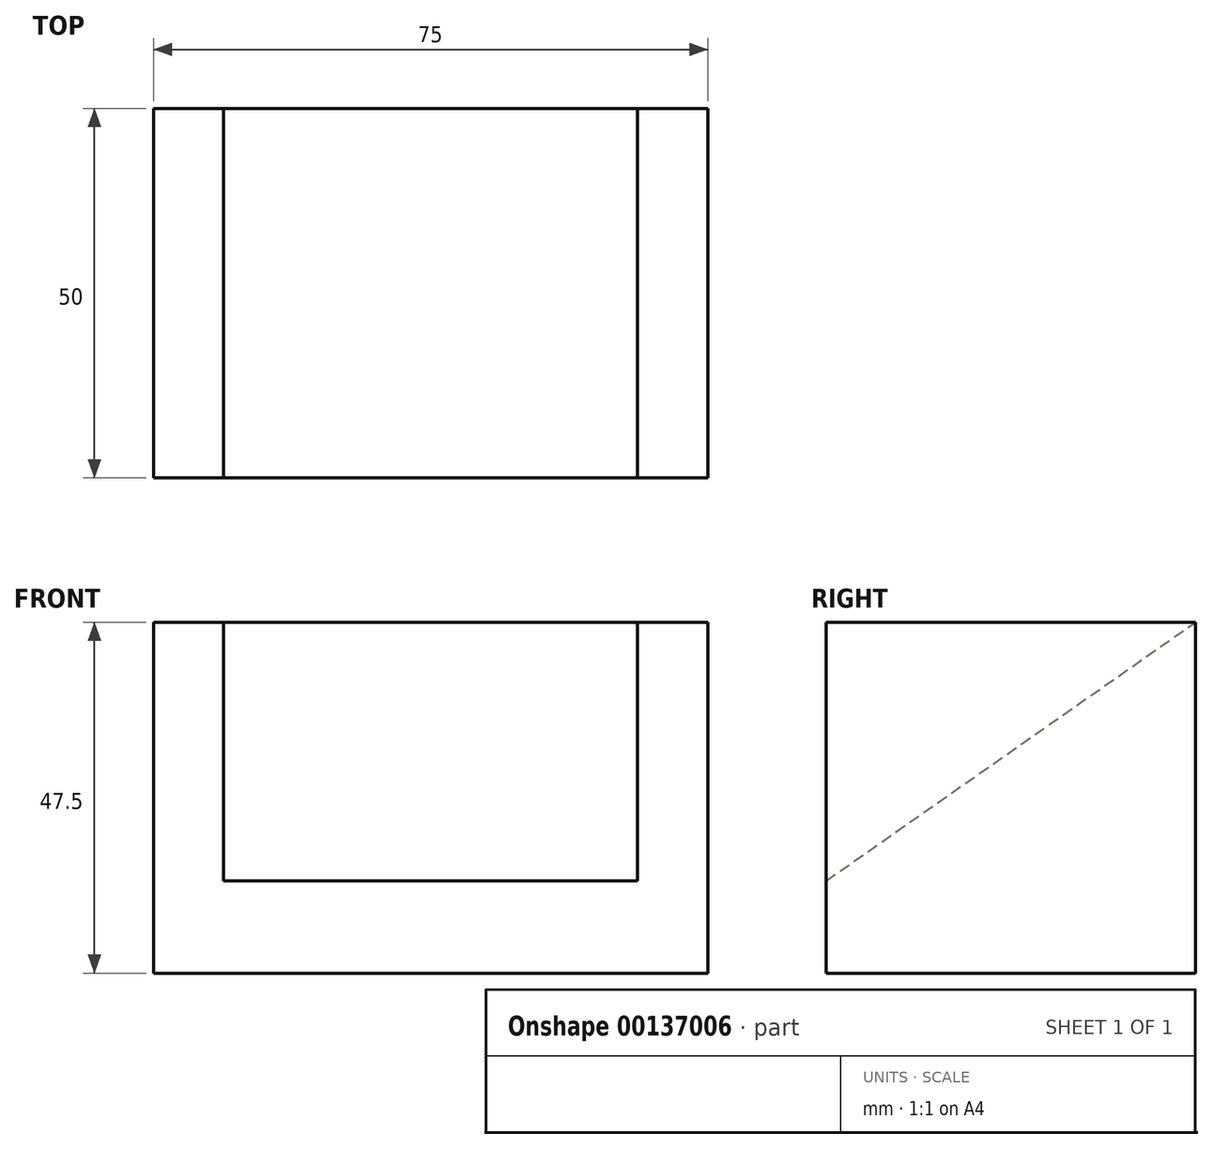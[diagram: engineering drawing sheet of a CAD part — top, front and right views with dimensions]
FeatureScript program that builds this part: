
annotation { "Feature Type Name" : "Feature", "Feature Type Description" : "" }
export const myFeature = defineFeature(function(context is Context, id is Id, definition is map)
    precondition{}
    {
        {
            var Q0;
            Q0=qCreatedBy(makeId("Front.planeOp"),FACE);
            var sketch = newSketch(context, id + "F0", { "sketchPlane" : qUnion([Q0])});
            skLineSegment(sketch, "E0.bottom", {"start": v(0, 0) * mm, "end": v(75, 0) * mm});
            skLineSegment(sketch, "E0.top", {"start": v(0, 47.5) * mm, "end": v(75, 47.5) * mm});
            skLineSegment(sketch, "E0.left", {"start": v(0, 0) * mm, "end": v(0, 47.5) * mm});
            skLineSegment(sketch, "E0.right", {"start": v(75, 0) * mm, "end": v(75, 47.5) * mm});
            skSolve(sketch);
        }
        {
            var Q0;
            Q0 = qSketchRegion(id + "F0", true);
            extrude(context, id + "F1", {"entities" : qUnion([Q0]), "depth" : 50 * mm});
        }
        {
            var Q0;
            Q0=makeQuery(id+"F1.opExtrude","CAP_EDGE",EDGE,{"disambiguationData":[OSD([sQuery(id+"F0.wireOp",EDGE,"E0.top")])],"isStart":true});
            cPlane(context, id + "F2", {"entities" : qUnion([Q0]), "cplaneType" : CPlaneType.LINE_ANGLE, "offset" : 25 * mm, "angle" : 35 * degree, "width" : 150 * mm, "height" : 150 * mm});
        }
        {
            var Q0;
            Q0=qCreatedBy(id+"F2.planeOp",FACE);
            var sketch = newSketch(context, id + "F3", { "sketchPlane" : qUnion([Q0])});
            skLineSegment(sketch, "E1.bottom", {"start": v(-65.5, 78.9) * mm, "end": v(-9.5, 78.9) * mm});
            skLineSegment(sketch, "E1.top", {"start": v(-65.5, 38.9) * mm, "end": v(-9.5, 38.9) * mm});
            skLineSegment(sketch, "E1.left", {"start": v(-65.5, 78.9) * mm, "end": v(-65.5, 38.9) * mm});
            skLineSegment(sketch, "E1.right", {"start": v(-9.5, 78.9) * mm, "end": v(-9.5, 38.9) * mm});
            skSolve(sketch);
        }
        {
            var Q0;
            Q0 = qSketchRegion(id + "F3", true);
            extrude(context, id + "F4", {"entities" : qUnion([Q0]), "operationType" : NewBodyOperationType.REMOVE, "endBound" : BoundingType.THROUGH_ALL, "oppositeDirection" : true, "depth" : 25 * mm});
        }
    });
